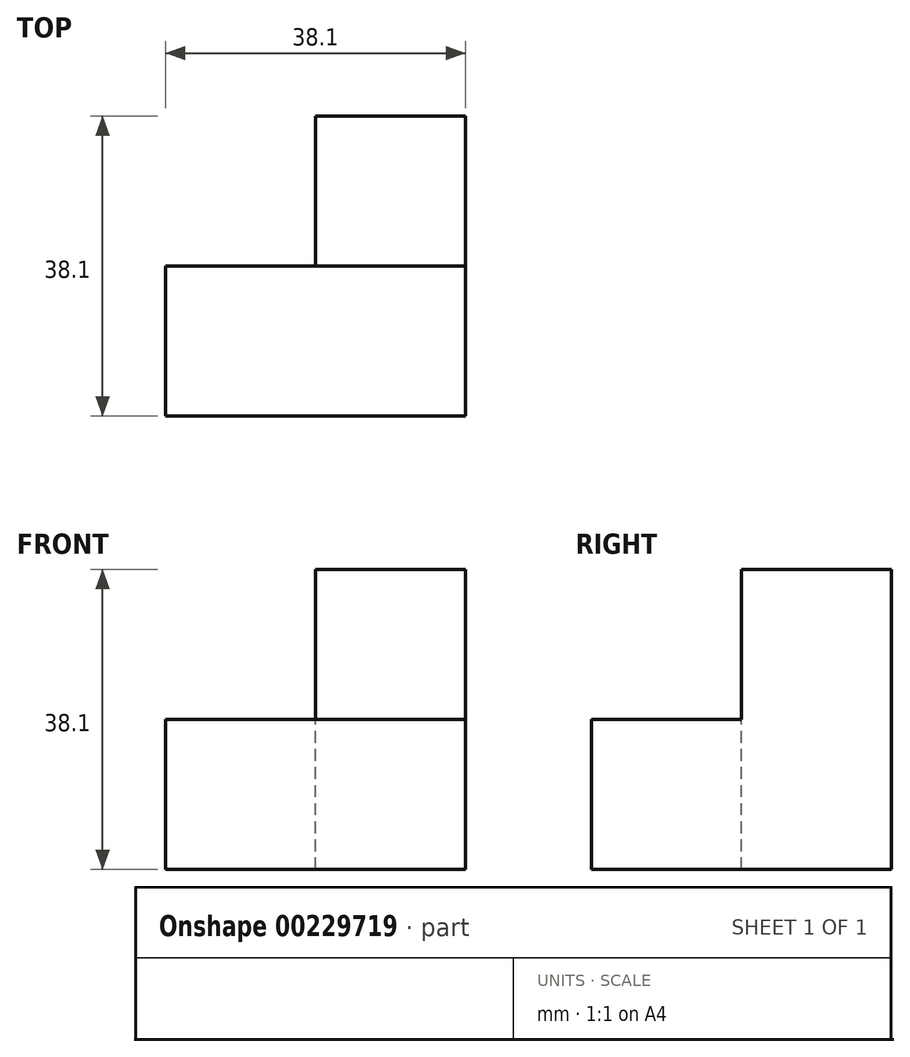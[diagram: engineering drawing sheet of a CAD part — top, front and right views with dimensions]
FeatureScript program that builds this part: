
annotation { "Feature Type Name" : "Feature", "Feature Type Description" : "" }
export const myFeature = defineFeature(function(context is Context, id is Id, definition is map)
    precondition{}
    {
        {
            var Q0;
            Q0=qCreatedBy(makeId("Front.planeOp"),FACE);
            var sketch = newSketch(context, id + "F0", { "sketchPlane" : qUnion([Q0])});
            skLineSegment(sketch, "E0.bottom", {"start": v(-24.38, 10.67) * mm, "end": v(13.72, 10.67) * mm});
            skLineSegment(sketch, "E0.top", {"start": v(-24.38, -8.38) * mm, "end": v(13.72, -8.38) * mm});
            skLineSegment(sketch, "E0.left", {"start": v(-24.38, 10.67) * mm, "end": v(-24.38, -8.38) * mm});
            skLineSegment(sketch, "E0.right", {"start": v(13.72, 10.67) * mm, "end": v(13.72, -8.38) * mm});
            skSolve(sketch);
        }
        {
            var Q0;
            Q0=makeQuery(id+"F0.imprint","IMPRINT",FACE,{"disambiguationData":[TD([[makeQuery(id+"F0.imprint","IMPRINT",EDGE,{"derivedFrom":sQuery(id+"F0.wireOp",EDGE,"E0.bottom")}),-1.0]])]});
            extrude(context, id + "F1", {"entities" : qUnion([Q0]), "depth" : 19.05 * mm});
        }
        {
            var Q0;
            Q0=makeQuery(id+"F1.opExtrude","SWEPT_FACE",FACE,{"disambiguationData":[OSD([sQuery(id+"F0.wireOp",EDGE,"E0.bottom")])]});
            var sketch = newSketch(context, id + "F2", { "sketchPlane" : qUnion([Q0])});
            skLineSegment(sketch, "E1.bottom", {"start": v(13.72, 0) * mm, "end": v(-5.33, 0) * mm});
            skLineSegment(sketch, "E1.top", {"start": v(13.72, 19.05) * mm, "end": v(-5.33, 19.05) * mm});
            skLineSegment(sketch, "E1.left", {"start": v(13.72, 0) * mm, "end": v(13.72, 19.05) * mm});
            skLineSegment(sketch, "E1.right", {"start": v(-5.33, 0) * mm, "end": v(-5.33, 19.05) * mm});
            skSolve(sketch);
        }
        {
            var Q0;
            Q0=makeQuery(id+"F2.imprint","IMPRINT",FACE,{"disambiguationData":[TD([[makeQuery(id+"F2.imprint","IMPRINT",EDGE,{"derivedFrom":sQuery(id+"F2.wireOp",EDGE,"E1.bottom")}),1.0]])]});
            extrude(context, id + "F3", {"entities" : qUnion([Q0]), "operationType" : NewBodyOperationType.ADD, "oppositeDirection" : true, "depth" : 19.05 * mm});
        }
        {
            var Q0;
            Q0=makeQuery(id+"F3.boolean.opBoolean","MERGE",FACE,{"derivedFrom":[makeQuery(id+"F1.opExtrude","SWEPT_FACE",FACE,{"disambiguationData":[OSD([sQuery(id+"F0.wireOp",EDGE,"E0.bottom")])]}),makeQuery(id+"F3.opExtrude","CAP_FACE",FACE,{"disambiguationData":[OSD([sQuery(id+"F2.wireOp",EDGE,"E1.bottom"),sQuery(id+"F2.wireOp",EDGE,"E1.top"),sQuery(id+"F2.wireOp",EDGE,"E1.left"),sQuery(id+"F2.wireOp",EDGE,"E1.right")])],"isStart":true})]});
            var sketch = newSketch(context, id + "F4", { "sketchPlane" : qUnion([Q0])});
            skLineSegment(sketch, "E2.bottom", {"start": v(-5.33, 0) * mm, "end": v(13.72, 0) * mm});
            skLineSegment(sketch, "E2.top", {"start": v(-5.33, 19.05) * mm, "end": v(13.72, 19.05) * mm});
            skLineSegment(sketch, "E2.left", {"start": v(-5.33, 0) * mm, "end": v(-5.33, 19.05) * mm});
            skLineSegment(sketch, "E2.right", {"start": v(13.72, 0) * mm, "end": v(13.72, 19.05) * mm});
            skSolve(sketch);
        }
        {
            var Q0;
            Q0=makeQuery(id+"F4.imprint","IMPRINT",FACE,{"disambiguationData":[TD([[makeQuery(id+"F4.imprint","IMPRINT",EDGE,{"derivedFrom":sQuery(id+"F4.wireOp",EDGE,"E2.bottom")}),1.0]])]});
            extrude(context, id + "F5", {"entities" : qUnion([Q0]), "operationType" : NewBodyOperationType.ADD, "depth" : 19.05 * mm});
        }
    });
